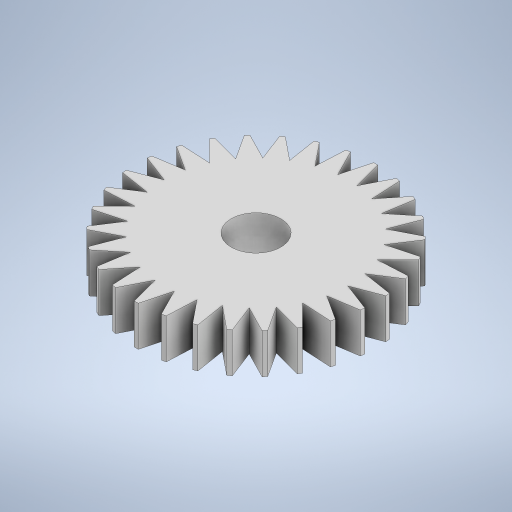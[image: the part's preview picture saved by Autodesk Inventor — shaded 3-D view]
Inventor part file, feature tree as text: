
AUTODESK INVENTOR PART (.ipt)
format: ipt  version: 2024 (Build 280153000, 153)  size: 357,888 bytes
history: native  units: mm
features: extrude x2, sketch x2
ambient origin geometry x8: Origin, YZ Plane, XZ Plane, XY Plane, X Axis, Y Axis, Z Axis, Center Point
bodies: Solid1 (feature_tree)
feature tree (4):
  extrude  "Extrusion1"  Depth=300.0mm TaperAngle=360.0deg
  extrude  "Extrusion4"  Depth=10.0mm TaperAngle=0.0deg
  sketch  "Sketch1"  dims[d0=30.0mm d1=300.0mm d3=360.0deg]
  sketch  "Sketch4"  dims[d5=5.0mm d6=0.0mm d15=10.0mm d16=0.0mm]
